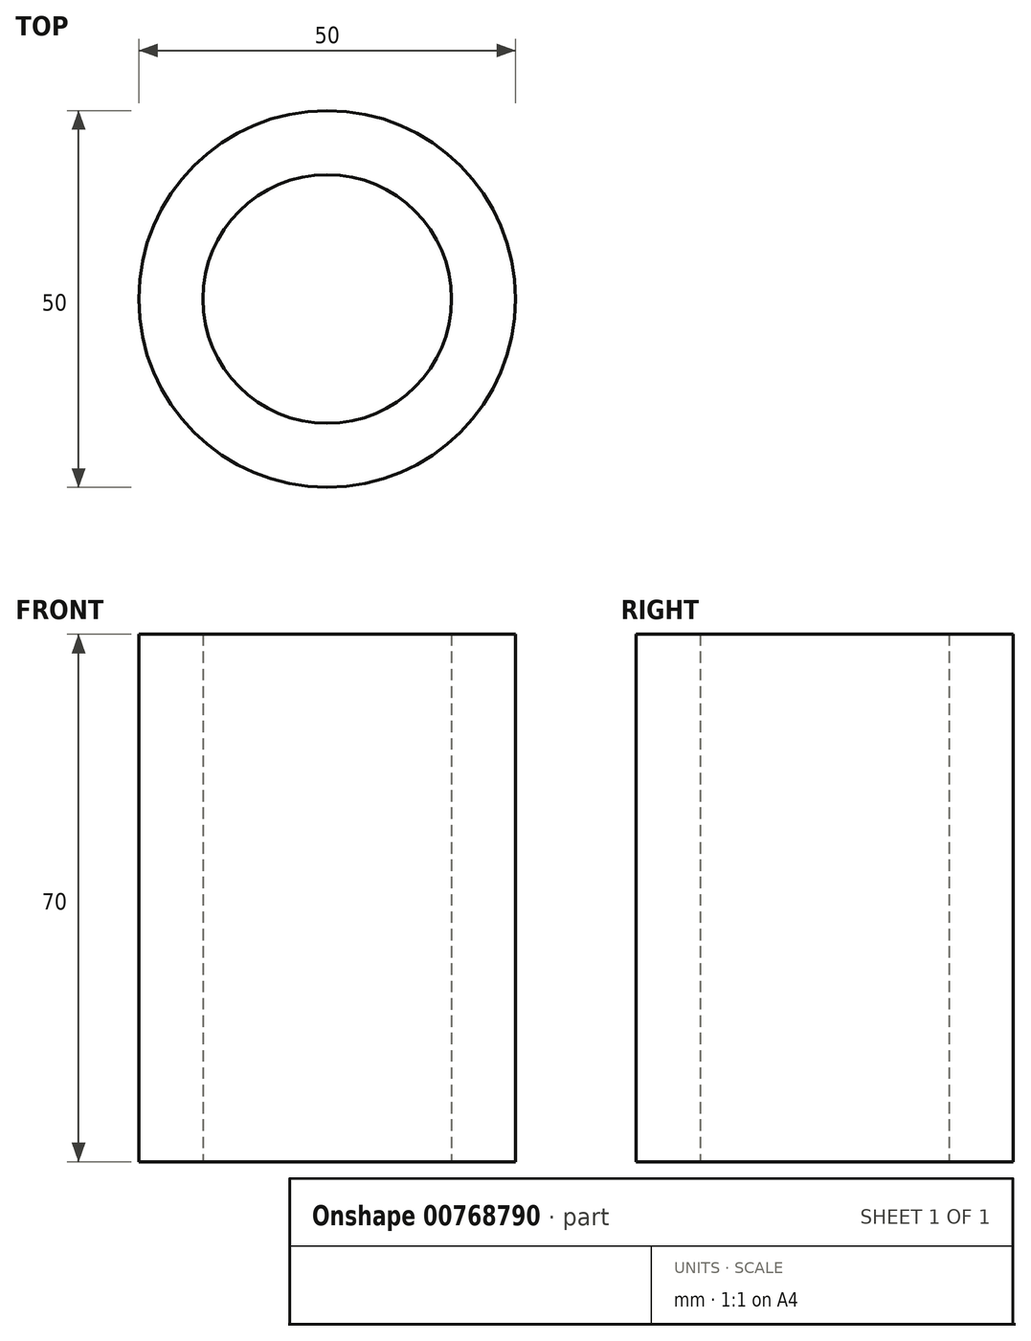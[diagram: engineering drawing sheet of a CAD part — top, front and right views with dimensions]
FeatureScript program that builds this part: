
annotation { "Feature Type Name" : "Feature", "Feature Type Description" : "" }
export const myFeature = defineFeature(function(context is Context, id is Id, definition is map)
    precondition{}
    {
        {
            var Q0;
            Q0=qCreatedBy(makeId("Top.planeOp"),FACE);
            var sketch = newSketch(context, id + "F0", { "sketchPlane" : qUnion([Q0])});
            skCircle(sketch, "E0", {"center": v(0, 0) * mm, "radius": 16.5 * mm});
            skCircle(sketch, "E1", {"center": v(0, 0) * mm, "radius": 25 * mm});
            skSolve(sketch);
        }
        {
            var Q0;
            Q0=makeQuery(id+"F0.imprint","IMPRINT",FACE,{"disambiguationData":[TD([[makeQuery(id+"F0.imprint","IMPRINT",EDGE,{"derivedFrom":sQuery(id+"F0.wireOp",EDGE,"E0")}),-1.0]])]});
            extrude(context, id + "F1", {"entities" : qUnion([Q0]), "depth" : 70 * mm, "offsetDistance" : 25 * mm});
        }
    });
